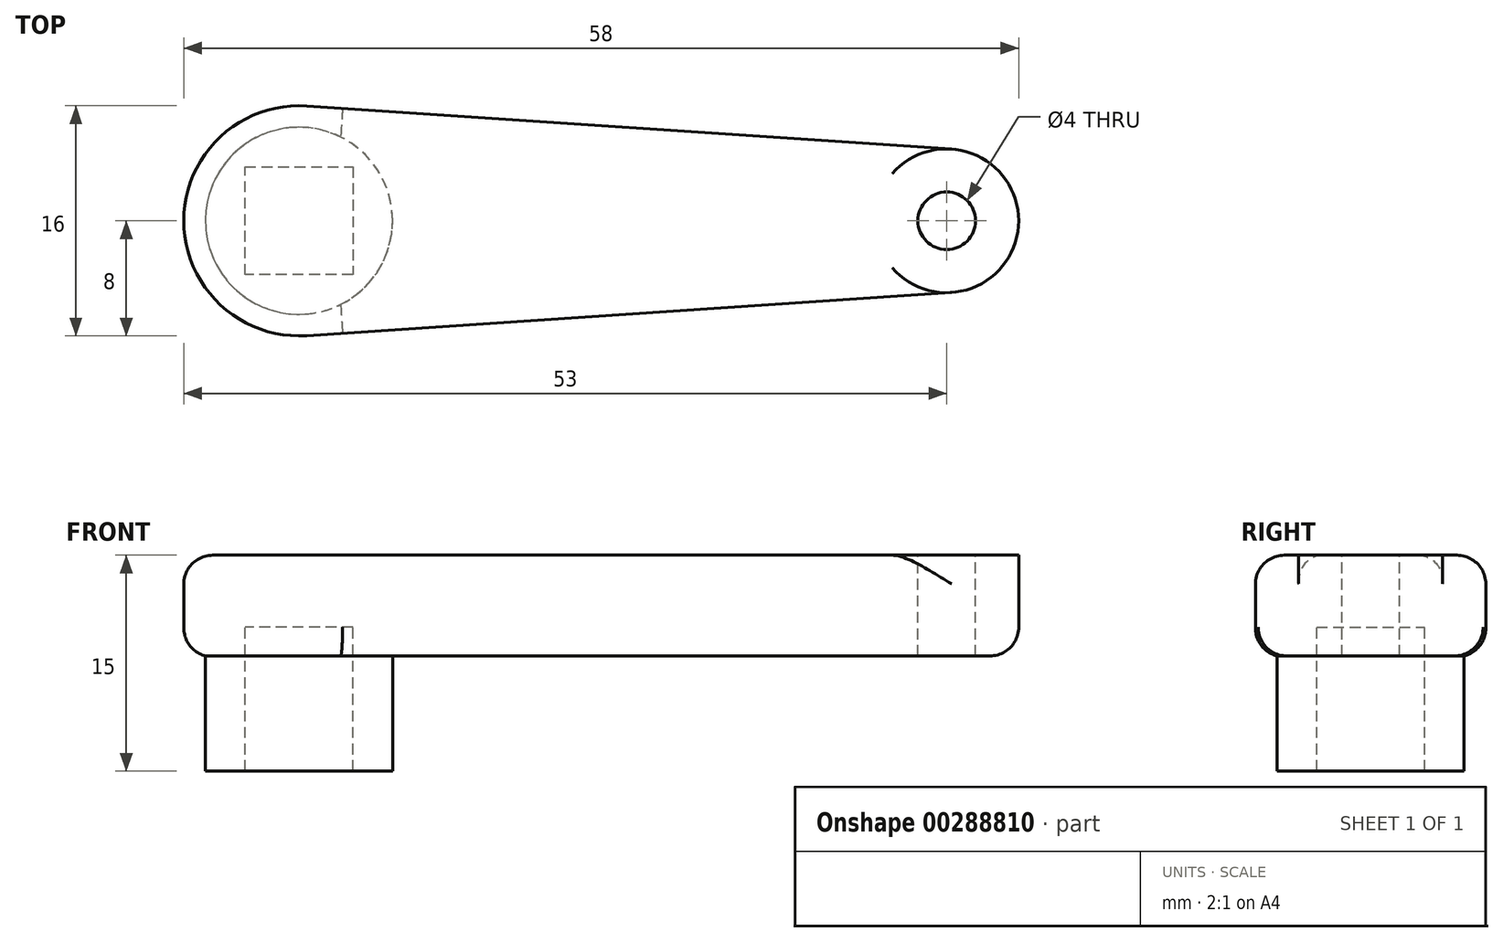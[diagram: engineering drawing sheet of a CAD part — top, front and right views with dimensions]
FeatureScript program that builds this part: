
annotation { "Feature Type Name" : "Feature", "Feature Type Description" : "" }
export const myFeature = defineFeature(function(context is Context, id is Id, definition is map)
    precondition{}
    {
        {
            var Q0;
            Q0=qCreatedBy(makeId("Top.planeOp"),FACE);
            var sketch = newSketch(context, id + "F0", { "sketchPlane" : qUnion([Q0])});
            skArc(sketch, "E0", {"start": v(0.53, 7.98) * mm, "mid": v(-8, 0) * mm, "end": v(0.53, -7.98) * mm});
            skLineSegment(sketch, "E1", {"start": v(0.53, 7.98) * mm, "end": v(45.33, 4.99) * mm});
            skLineSegment(sketch, "E2", {"start": v(0.53, -7.98) * mm, "end": v(45.33, -4.99) * mm});
            skArc(sketch, "E3", {"start": v(45.33, -4.99) * mm, "mid": v(50, 0) * mm, "end": v(45.33, 4.99) * mm});
            skSolve(sketch);
        }
        {
            var Q0;
            Q0=qSketchRegion(id+"F0",true);
            var Q1;
            Q1=makeQuery(id+"F0.imprint","IMPRINT",FACE,{"disambiguationData":[TD([[makeQuery(id+"F0.imprint","IMPRINT",EDGE,{"derivedFrom":sQuery(id+"F0.wireOp",EDGE,"E0")}),1.0]])]});
            extrude(context, id + "F1", {"entities" : qUnion([Q0, Q1]), "depth" : 7 * mm});
        }
        {
            var Q0;
            Q0=makeQuery(id+"F1.opExtrude","CAP_FACE",FACE,{"disambiguationData":[OSD([sQuery(id+"F0.wireOp",EDGE,"E0"),sQuery(id+"F0.wireOp",EDGE,"E1"),sQuery(id+"F0.wireOp",EDGE,"E2"),sQuery(id+"F0.wireOp",EDGE,"E3")])],"isStart":false});
            var sketch = newSketch(context, id + "F2", { "sketchPlane" : qUnion([Q0])});
            skCircle(sketch, "E4", {"center": v(0, 0) * mm, "radius": 6.5 * mm});
            skCircle(sketch, "E5", {"center": v(45, 0) * mm, "radius": 2 * mm});
            skCircle(sketch, "E6.cCircle", {"center": v(0, 0) * mm, "radius": 5.3 * mm, "construction": true});
            skLineSegment(sketch, "E6.0", {"start": v(-3.75, -3.75) * mm, "end": v(-3.75, 3.75) * mm});
            skLineSegment(sketch, "E6.1", {"start": v(-3.75, 3.75) * mm, "end": v(3.75, 3.75) * mm});
            skLineSegment(sketch, "E6.2", {"start": v(3.75, 3.75) * mm, "end": v(3.75, -3.75) * mm});
            skLineSegment(sketch, "E6.3", {"start": v(3.75, -3.75) * mm, "end": v(-3.75, -3.75) * mm});
            skCircle(sketch, "E7", {"center": v(45, 0) * mm, "radius": 5 * mm});
            skSolve(sketch);
        }
        {
            var Q0;
            Q0=makeQuery(id+"F2.imprint","IMPRINT",FACE,{"disambiguationData":[TD([[makeQuery(id+"F2.imprint","IMPRINT",EDGE,{"derivedFrom":sQuery(id+"F2.wireOp",EDGE,"E4")}),1.0]])]});
            extrude(context, id + "F3", {"entities" : qUnion([Q0]), "operationType" : NewBodyOperationType.ADD, "oppositeDirection" : true, "depth" : 15 * mm});
        }
        {
            var Q0;
            Q0=makeQuery(id+"F2.imprint","IMPRINT",FACE,{"disambiguationData":[TD([[makeQuery(id+"F2.imprint","IMPRINT",EDGE,{"derivedFrom":sQuery(id+"F2.wireOp",EDGE,"E5")}),1.0]])]});
            extrude(context, id + "F4", {"entities" : qUnion([Q0]), "operationType" : NewBodyOperationType.REMOVE, "oppositeDirection" : true, "depth" : 25 * mm});
        }
        {
            var Q0;
            Q0=makeQuery(id+"F2.imprint","IMPRINT",FACE,{"disambiguationData":[TD([[makeQuery(id+"F2.imprint","IMPRINT",EDGE,{"derivedFrom":sQuery(id+"F2.wireOp",EDGE,"E6.0")}),-1.0]])]});
            extrude(context, id + "F5", {"entities" : qUnion([Q0]), "operationType" : NewBodyOperationType.REMOVE, "endBound" : BoundingType.THROUGH_ALL, "oppositeDirection" : true, "depth" : 25 * mm, "hasSecondDirection" : true, "secondDirectionOppositeDirection" : true, "secondDirectionDepth" : 5 * mm});
        }
        {
            var Q0;
            Q0=makeQuery(id+"F1.opExtrude","CAP_EDGE",EDGE,{"disambiguationData":[OSD([sQuery(id+"F0.wireOp",EDGE,"E2")])],"isStart":false});
            var Q1;
            Q1=makeQuery(id+"F1.opExtrude","CAP_EDGE",EDGE,{"disambiguationData":[OSD([sQuery(id+"F0.wireOp",EDGE,"E1")])],"isStart":true});
            fillet(context, id + "F6", {"entities" : qUnion([Q0, Q1]), "radius" : 2 * mm, "tangentPropagation" : true, "allowEdgeOverflow" : false});
        }
        {
            var Q0;
            Q0=makeQuery(id+"F2.imprint","IMPRINT",FACE,{"disambiguationData":[TD([[makeQuery(id+"F2.imprint","IMPRINT",EDGE,{"derivedFrom":sQuery(id+"F2.wireOp",EDGE,"E5")}),-1.0]])]});
            extrude(context, id + "F7", {"entities" : qUnion([Q0]), "operationType" : NewBodyOperationType.ADD, "oppositeDirection" : true, "depth" : 2.8 * mm});
        }
    });
